# Revit family: Grohe_PlumbingFixtures_Eurosmart_SingleLeverBathMixer_33300003xxx
name_source: partatom
category: Plumbing Fixtures
revit_build: Autodesk Revit 2018 (Build: 20190510_1515(x64)
units: mm (PartAtom-declared; Revit-internal decimal feet)

## family parameters
Cut with Voids When Loaded = No
Host = Face
OmniClass Number = 23.65.00.00
OmniClass Title = Supply and Distribution of Liquids and Gases
Part Type = Normal
Room Calculation Point = No
Round Connector Dimension = Use Diameter
Shared = No

## types (1)
- 33300003
    Assembly Code = D2010
    AssetType = Fixed
    BIMObjectName = Grohe_PlumbingFixtures_Eurosmart_SingleLeverBathMixer_33300003
    CO2NeutralProduction = GROHE is one of the first leading manufacturer within the sanitary industry having a CO2-neutral production.
    CW Connection = Yes
    CWFU = 0
    ClassificationName = Uniclass 2015
    ClassificationValue = Pr_40_20_87_55
    Color = Chrome
    Default Elevation = 0 mm  [stored 0 ft]
    Description = With tactile operation and an automatic diverter, our new GROHE Eurosmart bath mixer has clean, modern lines and reliable, comfortable performance.
    DocumentationCertificates = https://www.bimstore.co
    DocumentationInstallationGuide = https://www.bimstore.co
    DocumentationLiterature = https://www.bimstore.co
    DocumentationMaintenance = https://www.bimstore.co
    DocumentationTechnical = https://www.bimstore.co
    DurationUnit = Year
    EF000003 = Wall
    EF000139 = Chromium-plated
    EF002149 = 0
    EF002286 = External thread
    EF002671 = Chrome
    EF007955 = 0
    EF011775 = EB
    EF011779 = 0
    EF012753 = 22
    EF014578 = 0
    EF014591 = 0
    EF020105 = No
    EF020259 = Downwards
    EF020780 = Single-grip
    EF020781 = Cartouche, ceramic
    EF020785 = 1/2 inch
    EF020789 = 189 mm
    EF020791 = Brass
    EF020799 = 0
    EF020805 = 0
    EF020967 = 0
    EF021035 = 0
    EF021808 = 2-hole
    EF021835 = 150 mm
    EF021855 = 0
    EF022042 = B
    EF022337 = 1/2 inch
    EF023686 = 0
    EF023687 = 0
    EF023688 = Foam jet nozzle
    EF023957 = 0
    EF024919 = 0
    EF025109 = Polished
    EFDE0022 = Group II, <=30 dB(A)
    EFNL0001 = 0
    EFSE0002 = 0
    Ecojoy = No
    ExpectedLife = 0
    Features = Wall mounted; GROHE SilkMove 35 mm ceramic cartridge; adjustable flow rate limiter; with temperature limiter; GROHE StarLight chrome finish; automatic diverter: bath/shower; mousseur; integrated non-return valve in shower outlet; S-unions; metal wall escutcheons; protected against backflow.
    FullRecyclabilityOfPlastic = All plastic components are fully recyclable
    GROHESocialCommittment = green.grohe.com/social_engagement
    GROHESustainability = green.grohe.com
    HW Connection = Yes
    HWFU = 0
    IfcExportAs = IfcPipeFitting
    IfcExportType = IfcPipeFittingType
    Keynote = N13
    Manufacturer = Grohe
    ManufacturerName = Grohe
    Model = 33300003
    ModelNumber = 33300003
    ModelReference = Single-Lever Bath Mixer 1/2"
    NBSDescription = Mixer taps
    NBSObjectName = Grohe - Mixer taps
    NBSReference = 45-35-70/345
    NominalDepth = 0 mm  [stored 0 ft]
    NominalHeight = 0 mm  [stored 0 ft]
    NominalLength = 0 mm  [stored 0 ft]
    PrimaryMaterial = Steel, Chrome Plated
    ProductionYear = 2021
    SustainabilityAward = green.grohe.com/awards
    SustainabilityReport = green.grohe.com/reporting
    Type Comments = Single-Lever Bath Mixer 1/2"
    TypeName = Single-Lever Bath Mixer 1/2"
    URL = https://www.grohe.co.uk
    Vent Connection = No
    WFU = 0
    WarrantyDurationLabor = 0
    WarrantyDurationParts = 0
    WarrantyDurationUnit = Year
    Waste Connection = No
    _BSBibleVersion = 16
    _BimSpecGuid = 0
    _CurrentRevision = 1
    _DistributedBy = www.bimstore.co
    _ObjectUserGuide = https://www.bimstore.co

note: [stored X ft] marks values corroborated as IEEE doubles in the binary element streams (Revit-internal decimal feet)

## geometry (parser evidence)
native form markers: Sweep x3
no freeform markers — native parametric forms only
